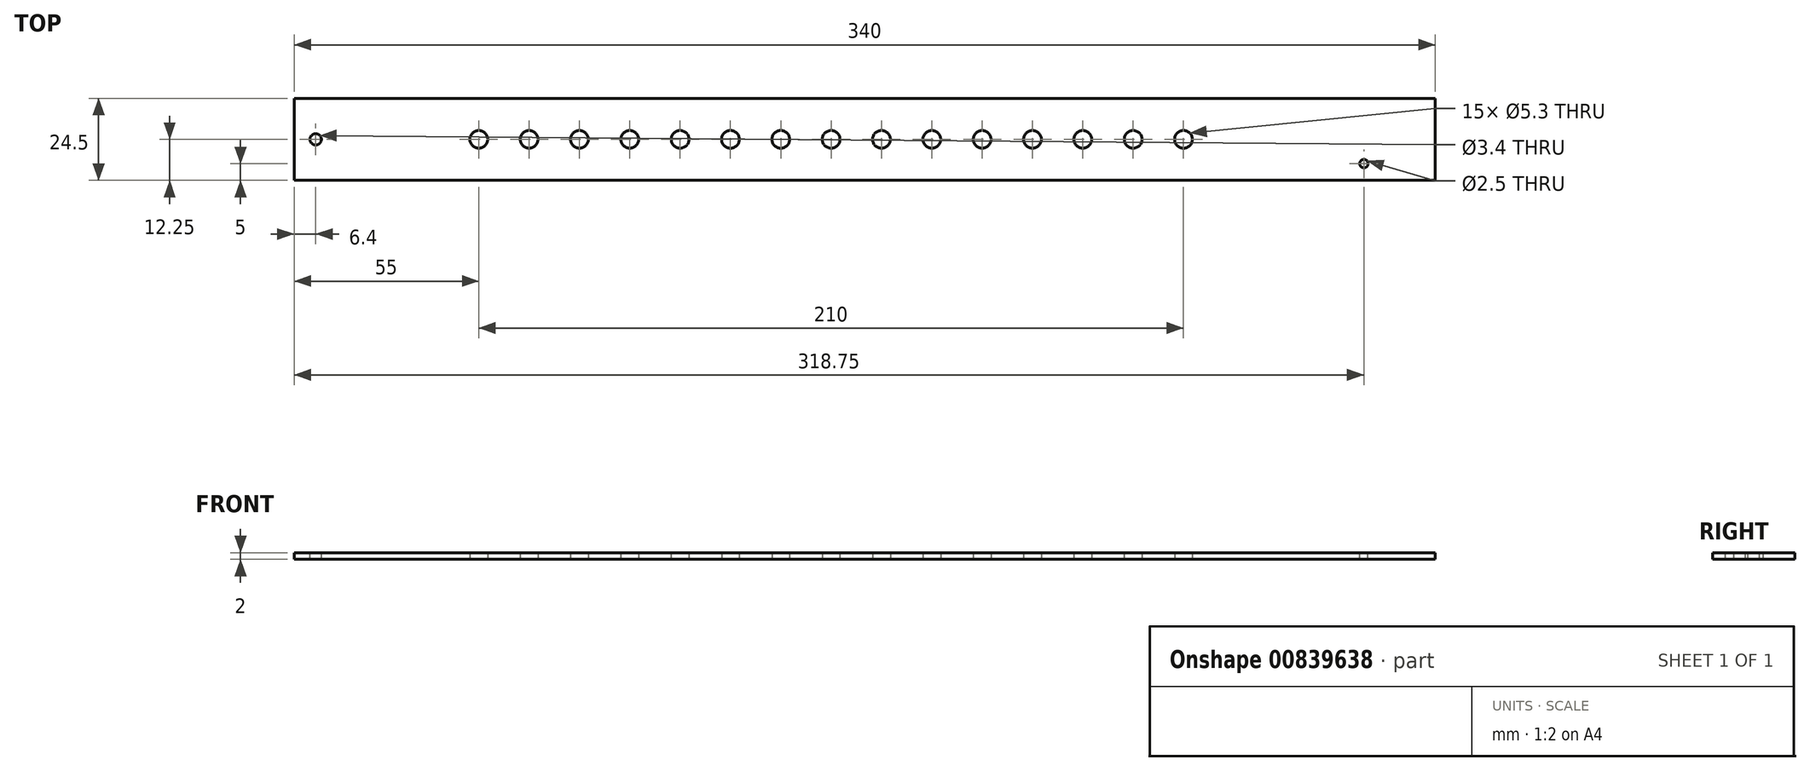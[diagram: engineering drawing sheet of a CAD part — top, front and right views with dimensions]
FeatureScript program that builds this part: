
annotation { "Feature Type Name" : "Feature", "Feature Type Description" : "" }
export const myFeature = defineFeature(function(context is Context, id is Id, definition is map)
    precondition{}
    {
        {
            var Q0;
            Q0=qCreatedBy(makeId("Top.planeOp"),FACE);
            var sketch = newSketch(context, id + "F0", { "sketchPlane" : qUnion([Q0])});
            skLineSegment(sketch, "E0.bottom", {"start": v(150, -12.25) * mm, "end": v(-150, -12.25) * mm});
            skLineSegment(sketch, "E0.top", {"start": v(150, 12.25) * mm, "end": v(-150, 12.25) * mm});
            skLineSegment(sketch, "E0.left", {"start": v(150, -12.25) * mm, "end": v(150, 12.25) * mm});
            skLineSegment(sketch, "E0.right", {"start": v(-150, -12.25) * mm, "end": v(-150, 12.25) * mm});
            skPoint(sketch, "E0.middle", {"position": v(0, 0) * mm});
            skCircle(sketch, "E1.2.0.0", {"center": v(-105, 0) * mm, "radius": 2.65 * mm});
            skCircle(sketch, "E1.3.0.0", {"center": v(-90, 0) * mm, "radius": 2.65 * mm});
            skCircle(sketch, "E1.4.0.0", {"center": v(-75, 0) * mm, "radius": 2.65 * mm});
            skCircle(sketch, "E1.5.0.0", {"center": v(-60, 0) * mm, "radius": 2.65 * mm});
            skCircle(sketch, "E1.6.0.0", {"center": v(-45, 0) * mm, "radius": 2.65 * mm});
            skCircle(sketch, "E1.7.0.0", {"center": v(-30, 0) * mm, "radius": 2.65 * mm});
            skCircle(sketch, "E1.8.0.0", {"center": v(-15, 0) * mm, "radius": 2.65 * mm});
            skCircle(sketch, "E1.9.0.0", {"center": v(0, 0) * mm, "radius": 2.65 * mm});
            skCircle(sketch, "E1.10.0.0", {"center": v(15, 0) * mm, "radius": 2.65 * mm});
            skCircle(sketch, "E1.11.0.0", {"center": v(30, 0) * mm, "radius": 2.65 * mm});
            skCircle(sketch, "E1.12.0.0", {"center": v(45, 0) * mm, "radius": 2.65 * mm});
            skCircle(sketch, "E1.13.0.0", {"center": v(60, 0) * mm, "radius": 2.65 * mm});
            skCircle(sketch, "E1.14.0.0", {"center": v(75, 0) * mm, "radius": 2.65 * mm});
            skCircle(sketch, "E1.15.0.0", {"center": v(90, 0) * mm, "radius": 2.65 * mm});
            skCircle(sketch, "E1.16.0.0", {"center": v(105, 0) * mm, "radius": 2.65 * mm});
            skLineSegment(sketch, "E1.direction1", {"start": v(-135, 0) * mm, "end": v(-120, 0) * mm, "construction": true});
            skSolve(sketch);
        }
        {
            var Q0;
            Q0=makeQuery(id+"F0.imprint","IMPRINT",FACE,{"disambiguationData":[TD([[makeQuery(id+"F0.imprint","IMPRINT",EDGE,{"derivedFrom":sQuery(id+"F0.wireOp",EDGE,"E0.bottom")}),-1.0]])]});
            extrude(context, id + "F1", {"entities" : qUnion([Q0]), "depth" : 2 * mm, "offsetDistance" : 25 * mm});
        }
        {
            var Q0;
            Q0=makeQuery(id+"F1.opExtrude","SWEPT_FACE",FACE,{"disambiguationData":[OSD([sQuery(id+"F0.wireOp",EDGE,"E0.right")])]});
            extrude(context, id + "F2", {"entities" : qUnion([Q0]), "operationType" : NewBodyOperationType.ADD, "depth" : 10 * mm, "offsetDistance" : 25 * mm});
        }
        {
            var Q0;
            Q0=makeQuery(id+"F1.opExtrude","SWEPT_FACE",FACE,{"disambiguationData":[OSD([sQuery(id+"F0.wireOp",EDGE,"E0.left")])]});
            extrude(context, id + "F3", {"entities" : qUnion([Q0]), "operationType" : NewBodyOperationType.ADD, "depth" : 30 * mm, "offsetDistance" : 25 * mm});
        }
        {
            var Q0;
            {var subQ0=sQuery(id+"F0.wireOp",EDGE,"E0.left");var subQ1=sQuery(id+"F0.wireOp",EDGE,"E0.right");Q0=makeQuery(id+"F3.boolean.opBoolean","MERGE",FACE,{"derivedFrom":[makeQuery(id+"F2.boolean.opBoolean","MERGE",FACE,{"derivedFrom":[makeQuery(id+"F1.opExtrude","CAP_FACE",FACE,{"disambiguationData":[OSD([sQuery(id+"F0.wireOp",EDGE,"E0.bottom"),sQuery(id+"F0.wireOp",EDGE,"E0.top"),subQ0,subQ1,sQuery(id+"F0.wireOp",EDGE,"LckrCdrf-Oz9b-iWqB-HkfW-gHpTPrbceAxr"),sQuery(id+"F0.wireOp",EDGE,"E1.1.0.0"),sQuery(id+"F0.wireOp",EDGE,"E1.2.0.0"),sQuery(id+"F0.wireOp",EDGE,"E1.3.0.0"),sQuery(id+"F0.wireOp",EDGE,"E1.4.0.0"),sQuery(id+"F0.wireOp",EDGE,"E1.5.0.0"),sQuery(id+"F0.wireOp",EDGE,"E1.6.0.0"),sQuery(id+"F0.wireOp",EDGE,"E1.7.0.0"),sQuery(id+"F0.wireOp",EDGE,"E1.8.0.0"),sQuery(id+"F0.wireOp",EDGE,"E1.9.0.0"),sQuery(id+"F0.wireOp",EDGE,"E1.10.0.0"),sQuery(id+"F0.wireOp",EDGE,"E1.11.0.0"),sQuery(id+"F0.wireOp",EDGE,"E1.12.0.0"),sQuery(id+"F0.wireOp",EDGE,"E1.13.0.0"),sQuery(id+"F0.wireOp",EDGE,"E1.14.0.0"),sQuery(id+"F0.wireOp",EDGE,"E1.15.0.0"),sQuery(id+"F0.wireOp",EDGE,"E1.16.0.0"),sQuery(id+"F0.wireOp",EDGE,"E1.17.0.0"),sQuery(id+"F0.wireOp",EDGE,"E1.18.0.0")])],"isStart":false}),makeQuery(id+"F2.opExtrude","SWEPT_FACE",FACE,{"disambiguationData":[OSD([subQ1]),TDD([makeQuery(id+"F1.opExtrude","CAP_EDGE",EDGE,{"disambiguationData":[OSD([subQ1])],"isStart":false})])]})]}),makeQuery(id+"F3.opExtrude","SWEPT_FACE",FACE,{"disambiguationData":[OSD([subQ0]),TDD([makeQuery(id+"F1.opExtrude","CAP_EDGE",EDGE,{"disambiguationData":[OSD([subQ0])],"isStart":false})])]})]});}
            var sketch = newSketch(context, id + "F4", { "sketchPlane" : qUnion([Q0])});
            skCircle(sketch, "E2", {"center": v(-153.6, 0) * mm, "radius": 1.7 * mm});
            skSolve(sketch);
        }
        {
            var Q0;
            Q0=makeQuery(id+"F4.imprint","IMPRINT",FACE,{"disambiguationData":[TD([[makeQuery(id+"F4.imprint","IMPRINT",EDGE,{"derivedFrom":sQuery(id+"F4.wireOp",EDGE,"E2")}),1.0]])]});
            extrude(context, id + "F5", {"entities" : qUnion([Q0]), "operationType" : NewBodyOperationType.REMOVE, "endBound" : BoundingType.UP_TO_NEXT, "oppositeDirection" : true, "depth" : 25 * mm, "offsetDistance" : 25 * mm});
        }
        {
            var Q0;
            {var subQ0=sQuery(id+"F0.wireOp",EDGE,"E0.left");var subQ1=sQuery(id+"F0.wireOp",EDGE,"E0.right");Q0=makeQuery(id+"F3.boolean.opBoolean","MERGE",FACE,{"derivedFrom":[makeQuery(id+"F2.boolean.opBoolean","MERGE",FACE,{"derivedFrom":[makeQuery(id+"F1.opExtrude","CAP_FACE",FACE,{"disambiguationData":[OSD([sQuery(id+"F0.wireOp",EDGE,"E0.bottom"),sQuery(id+"F0.wireOp",EDGE,"E0.top"),subQ0,subQ1,sQuery(id+"F0.wireOp",EDGE,"LckrCdrf-Oz9b-iWqB-HkfW-gHpTPrbceAxr"),sQuery(id+"F0.wireOp",EDGE,"E1.1.0.0"),sQuery(id+"F0.wireOp",EDGE,"E1.2.0.0"),sQuery(id+"F0.wireOp",EDGE,"E1.3.0.0"),sQuery(id+"F0.wireOp",EDGE,"E1.4.0.0"),sQuery(id+"F0.wireOp",EDGE,"E1.5.0.0"),sQuery(id+"F0.wireOp",EDGE,"E1.6.0.0"),sQuery(id+"F0.wireOp",EDGE,"E1.7.0.0"),sQuery(id+"F0.wireOp",EDGE,"E1.8.0.0"),sQuery(id+"F0.wireOp",EDGE,"E1.9.0.0"),sQuery(id+"F0.wireOp",EDGE,"E1.10.0.0"),sQuery(id+"F0.wireOp",EDGE,"E1.11.0.0"),sQuery(id+"F0.wireOp",EDGE,"E1.12.0.0"),sQuery(id+"F0.wireOp",EDGE,"E1.13.0.0"),sQuery(id+"F0.wireOp",EDGE,"E1.14.0.0"),sQuery(id+"F0.wireOp",EDGE,"E1.15.0.0"),sQuery(id+"F0.wireOp",EDGE,"E1.16.0.0"),sQuery(id+"F0.wireOp",EDGE,"E1.17.0.0"),sQuery(id+"F0.wireOp",EDGE,"E1.18.0.0")])],"isStart":false}),makeQuery(id+"F2.opExtrude","SWEPT_FACE",FACE,{"disambiguationData":[OSD([subQ1]),TDD([makeQuery(id+"F1.opExtrude","CAP_EDGE",EDGE,{"disambiguationData":[OSD([subQ1])],"isStart":false})])]})]}),makeQuery(id+"F3.opExtrude","SWEPT_FACE",FACE,{"disambiguationData":[OSD([subQ0]),TDD([makeQuery(id+"F1.opExtrude","CAP_EDGE",EDGE,{"disambiguationData":[OSD([subQ0])],"isStart":false})])]})]});}
            var sketch = newSketch(context, id + "F6", { "sketchPlane" : qUnion([Q0])});
            skCircle(sketch, "E3", {"center": v(158.75, -7.25) * mm, "radius": 1.25 * mm});
            skSolve(sketch);
        }
        {
            var Q0;
            Q0=makeQuery(id+"F6.imprint","IMPRINT",FACE,{"disambiguationData":[TD([[makeQuery(id+"F6.imprint","IMPRINT",EDGE,{"derivedFrom":sQuery(id+"F6.wireOp",EDGE,"E3")}),1.0]])]});
            extrude(context, id + "F7", {"entities" : qUnion([Q0]), "operationType" : NewBodyOperationType.REMOVE, "endBound" : BoundingType.UP_TO_NEXT, "oppositeDirection" : true, "depth" : 25 * mm, "offsetDistance" : 25 * mm});
        }
    });
